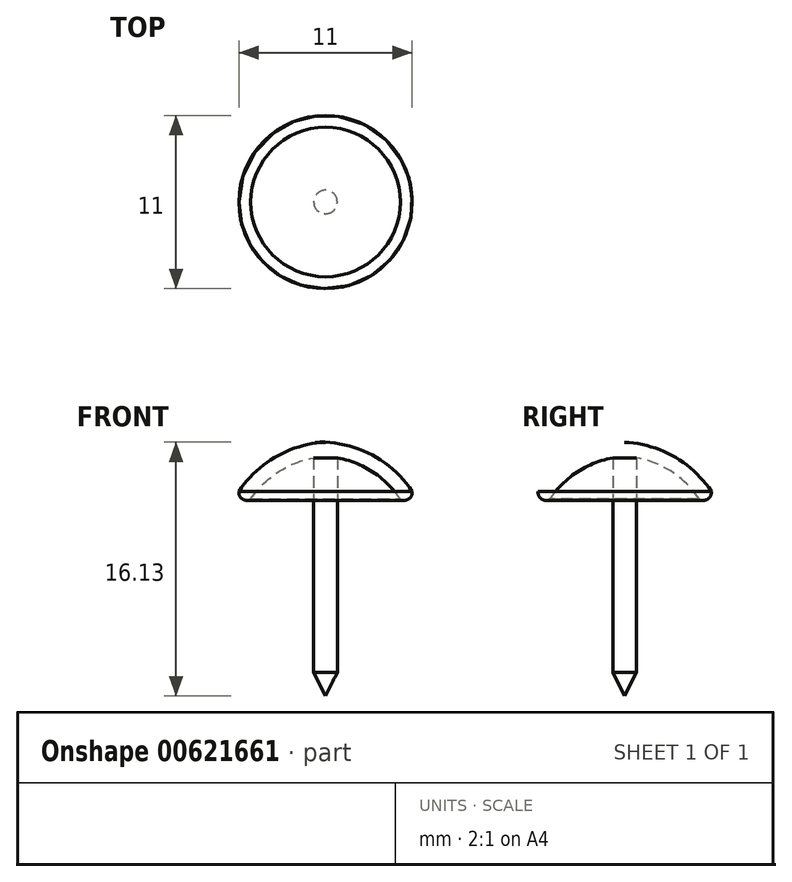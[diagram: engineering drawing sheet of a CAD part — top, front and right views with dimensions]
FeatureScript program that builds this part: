
annotation { "Feature Type Name" : "Feature", "Feature Type Description" : "" }
export const myFeature = defineFeature(function(context is Context, id is Id, definition is map)
    precondition{}
    {
        {
            var Q0;
            Q0=qCreatedBy(makeId("Front.planeOp"),FACE);
            var sketch = newSketch(context, id + "F0", { "sketchPlane" : qUnion([Q0])});
            skArc(sketch, "E0", {"start": v(0, 3.12) * mm, "mid": v(-3.12, 2.22) * mm, "end": v(-5.5, 0) * mm});
            skArc(sketch, "E1.0", {"start": v(0, 2.22) * mm, "mid": v(-2.7, 1.43) * mm, "end": v(-4.75, -0.5) * mm});
            skArc(sketch, "E2", {"start": v(-5.5, 0) * mm, "mid": v(-5.28, -0.48) * mm, "end": v(-4.75, -0.5) * mm});
            skLineSegment(sketch, "E3", {"start": v(0, -0.12) * mm, "end": v(0, 3.52) * mm});
            skSolve(sketch);
        }
        {
            var Q0;
            Q0=qCreatedBy(makeId("Front.planeOp"),FACE);
            var sketch = newSketch(context, id + "F1", { "sketchPlane" : qUnion([Q0])});
            skLineSegment(sketch, "E4", {"start": v(0, 0) * mm, "end": v(0, 6.71) * mm, "construction": true});
            skSolve(sketch);
        }
        {
            var Q0;
            {var subQ0=sQuery(id+"F0.wireOp",EDGE,"E0");Q0=makeQuery(id+"F0.imprint","IMPRINT",FACE,{"disambiguationData":[TD([[makeQuery(id+"F0.imprint","IMPRINT",EDGE,{"derivedFrom":subQ0}),1.0]])]});}
            var Q1;
            Q1 = qConstructionFilter(qBodyType(qCreatedBy(id + "F0" ,EDGE), BodyType.WIRE), ConstructionObject.NO);
            var Q2;
            Q2=sQuery(id+"F1.wireOp",EDGE,"E4");
            revolve(context, id + "F2", {"entities" : qUnion([Q0]), "surfaceEntities" : qUnion([Q1]), "axis" : qUnion([Q2]), "revolveType" : RevolveType.FULL});
        }
        {
            var Q0;
            Q0=qCreatedBy(makeId("Front.planeOp"),FACE);
            var sketch = newSketch(context, id + "F3", { "sketchPlane" : qUnion([Q0])});
            skLineSegment(sketch, "E5", {"start": v(0, 3) * mm, "end": v(0, -13) * mm});
            skLineSegment(sketch, "E6.0", {"start": v(-0.75, 3) * mm, "end": v(-0.75, -11.5) * mm});
            skLineSegment(sketch, "E7", {"start": v(-0.75, -11.5) * mm, "end": v(0, -13) * mm});
            skLineSegment(sketch, "E8", {"start": v(0, -13) * mm, "end": v(0, -13) * mm});
            skLineSegment(sketch, "E9", {"start": v(-0.75, 3) * mm, "end": v(0, 3) * mm});
            skSolve(sketch);
        }
        {
            var Q0;
            Q0=makeQuery(id+"F3.imprint","IMPRINT",FACE,{"disambiguationData":[TD([[makeQuery(id+"F3.imprint","IMPRINT",EDGE,{"derivedFrom":sQuery(id+"F3.wireOp",EDGE,"E5")}),-1.0]])]});
            var Q1;
            Q1=sQuery(id+"F1.wireOp",EDGE,"E4");
            revolve(context, id + "F4", {"operationType" : NewBodyOperationType.ADD, "entities" : qUnion([Q0]), "axis" : qUnion([Q1]), "revolveType" : RevolveType.FULL});
        }
    });
